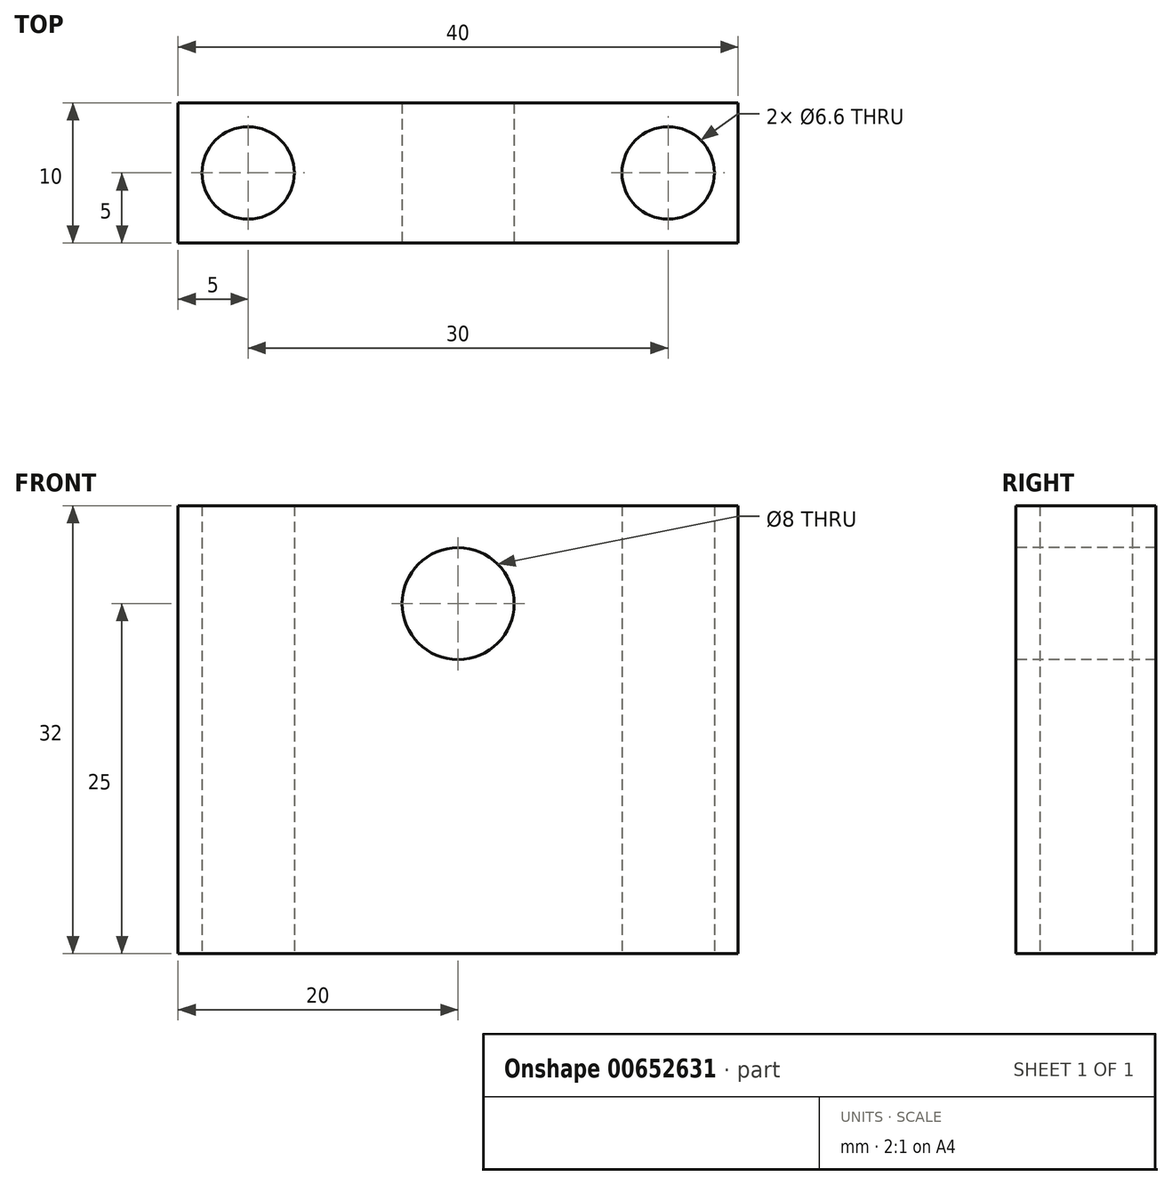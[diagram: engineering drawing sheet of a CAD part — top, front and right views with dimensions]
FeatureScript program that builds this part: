
annotation { "Feature Type Name" : "Feature", "Feature Type Description" : "" }
export const myFeature = defineFeature(function(context is Context, id is Id, definition is map)
    precondition{}
    {
        {
            var Q0;
            Q0=qCreatedBy(makeId("Front.planeOp"),FACE);
            var sketch = newSketch(context, id + "F0", { "sketchPlane" : qUnion([Q0])});
            skLineSegment(sketch, "E0", {"start": v(-20, 0) * mm, "end": v(20, 0) * mm});
            skLineSegment(sketch, "E1", {"start": v(20, 0) * mm, "end": v(20, 32) * mm});
            skLineSegment(sketch, "E2", {"start": v(20, 32) * mm, "end": v(-20, 32) * mm});
            skLineSegment(sketch, "E3", {"start": v(-20, 32) * mm, "end": v(-20, 0) * mm});
            skCircle(sketch, "E4", {"center": v(0, 25) * mm, "radius": 4 * mm});
            skSolve(sketch);
        }
        {
            var Q0;
            Q0=qSketchRegion(id+"F0",true);
            extrude(context, id + "F1", {"entities" : qUnion([Q0]), "oppositeDirection" : true, "depth" : 10 * mm, "offsetDistance" : 25 * mm});
        }
        {
            var Q0;
            Q0=makeQuery(id+"F1.opExtrude","SWEPT_FACE",FACE,{"disambiguationData":[OSD([sQuery(id+"F0.wireOp",EDGE,"E0")])]});
            var sketch = newSketch(context, id + "F2", { "sketchPlane" : qUnion([Q0])});
            skCircle(sketch, "E5", {"center": v(-15, -5) * mm, "radius": 3.3 * mm});
            skCircle(sketch, "E6", {"center": v(15, -5) * mm, "radius": 3.3 * mm});
            skSolve(sketch);
        }
        {
            var Q0;
            Q0=makeQuery(id+"F2.imprint","IMPRINT",FACE,{"disambiguationData":[TD([[makeQuery(id+"F2.imprint","IMPRINT",EDGE,{"derivedFrom":sQuery(id+"F2.wireOp",EDGE,"E5")}),1.0]])]});
            var Q1;
            Q1=makeQuery(id+"F2.imprint","IMPRINT",FACE,{"disambiguationData":[TD([[makeQuery(id+"F2.imprint","IMPRINT",EDGE,{"derivedFrom":sQuery(id+"F2.wireOp",EDGE,"E6")}),1.0]])]});
            extrude(context, id + "F3", {"entities" : qUnion([Q0, Q1]), "operationType" : NewBodyOperationType.REMOVE, "endBound" : BoundingType.UP_TO_NEXT, "oppositeDirection" : true, "depth" : 10 * mm, "offsetDistance" : 25 * mm});
        }
    });
